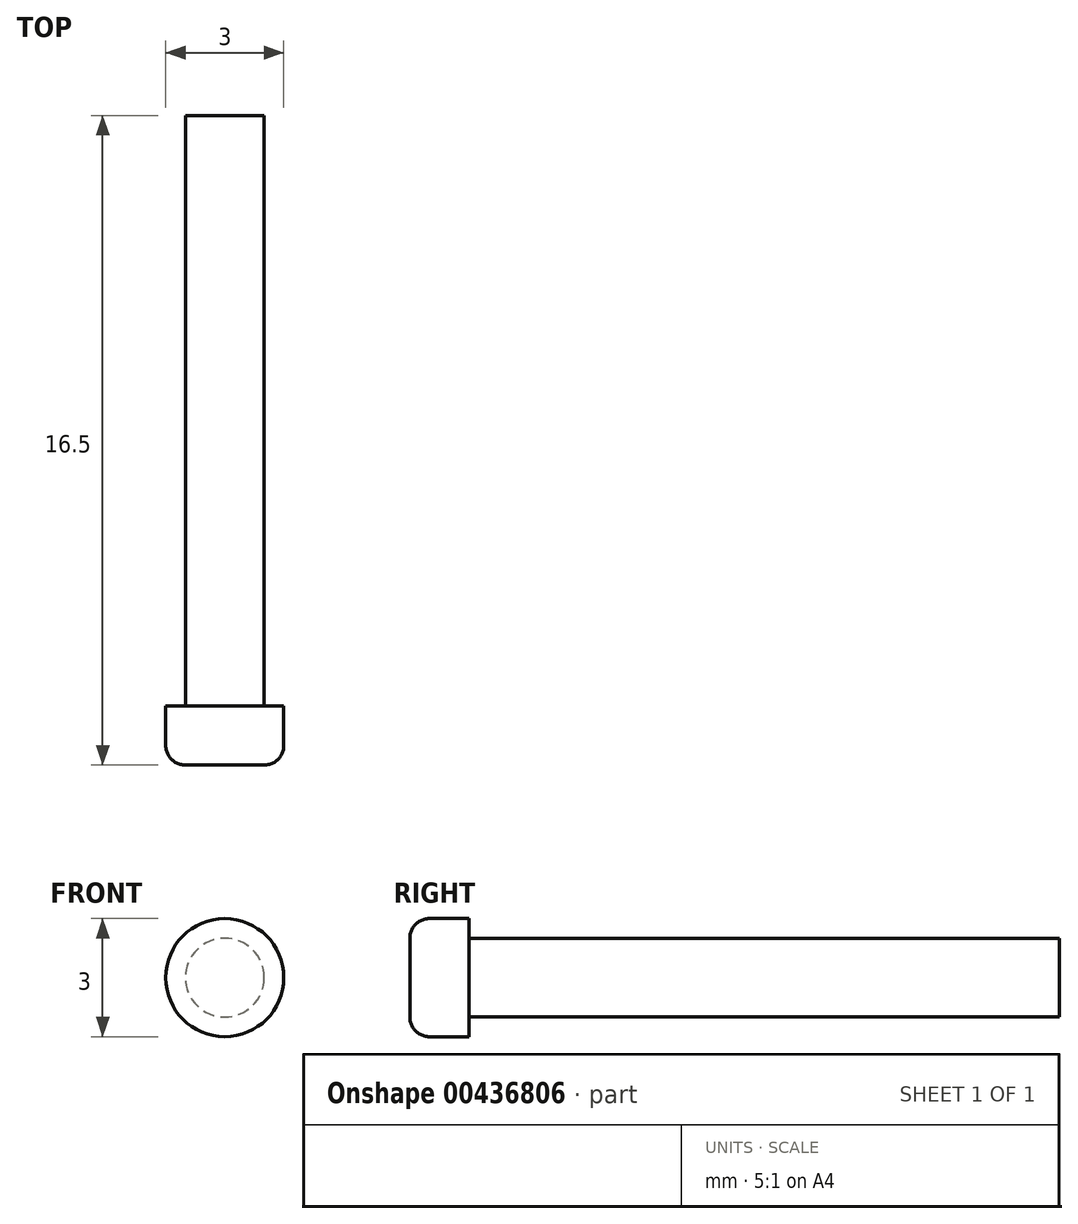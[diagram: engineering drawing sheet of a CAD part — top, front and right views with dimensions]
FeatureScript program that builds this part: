
annotation { "Feature Type Name" : "Feature", "Feature Type Description" : "" }
export const myFeature = defineFeature(function(context is Context, id is Id, definition is map)
    precondition{}
    {
        {
            var Q0;
            Q0=qCreatedBy(makeId("Front.planeOp"),FACE);
            var sketch = newSketch(context, id + "F0", { "sketchPlane" : qUnion([Q0])});
            skCircle(sketch, "E0", {"center": v(0, 0) * mm, "radius": 1.5 * mm});
            skSolve(sketch);
        }
        {
            var Q0;
            Q0=makeQuery(id+"F0.imprint","IMPRINT",FACE,{"disambiguationData":[TD([[makeQuery(id+"F0.imprint","IMPRINT",EDGE,{"derivedFrom":sQuery(id+"F0.wireOp",EDGE,"E0")}),1.0]])]});
            extrude(context, id + "F1", {"entities" : qUnion([Q0]), "depth" : 1.5 * mm});
        }
        {
            var Q0;
            Q0=makeQuery(id+"F1.opExtrude","CAP_EDGE",EDGE,{"disambiguationData":[OSD([sQuery(id+"F0.wireOp",EDGE,"E0")])],"isStart":false});
            fillet(context, id + "F2", {"entities" : qUnion([Q0]), "radius" : 0.5 * mm, "tangentPropagation" : true, "allowEdgeOverflow" : false});
        }
        {
            var Q0;
            Q0=makeQuery(id+"F1.opExtrude","CAP_FACE",FACE,{"disambiguationData":[OSD([sQuery(id+"F0.wireOp",EDGE,"E0")])],"isStart":true});
            var sketch = newSketch(context, id + "F3", { "sketchPlane" : qUnion([Q0])});
            skCircle(sketch, "E1", {"center": v(0, 0) * mm, "radius": 1 * mm});
            skSolve(sketch);
        }
        {
            var Q0;
            Q0=makeQuery(id+"F3.imprint","IMPRINT",FACE,{"disambiguationData":[TD([[makeQuery(id+"F3.imprint","IMPRINT",EDGE,{"derivedFrom":sQuery(id+"F3.wireOp",EDGE,"E1")}),1.0]])]});
            var Q1;
            Q1=sQuery(id+"F3.wireOp",EDGE,"E1");
            extrude(context, id + "F4", {"entities" : qUnion([Q0]), "surfaceEntities" : qUnion([Q1]), "depth" : 15 * mm});
        }
    });
